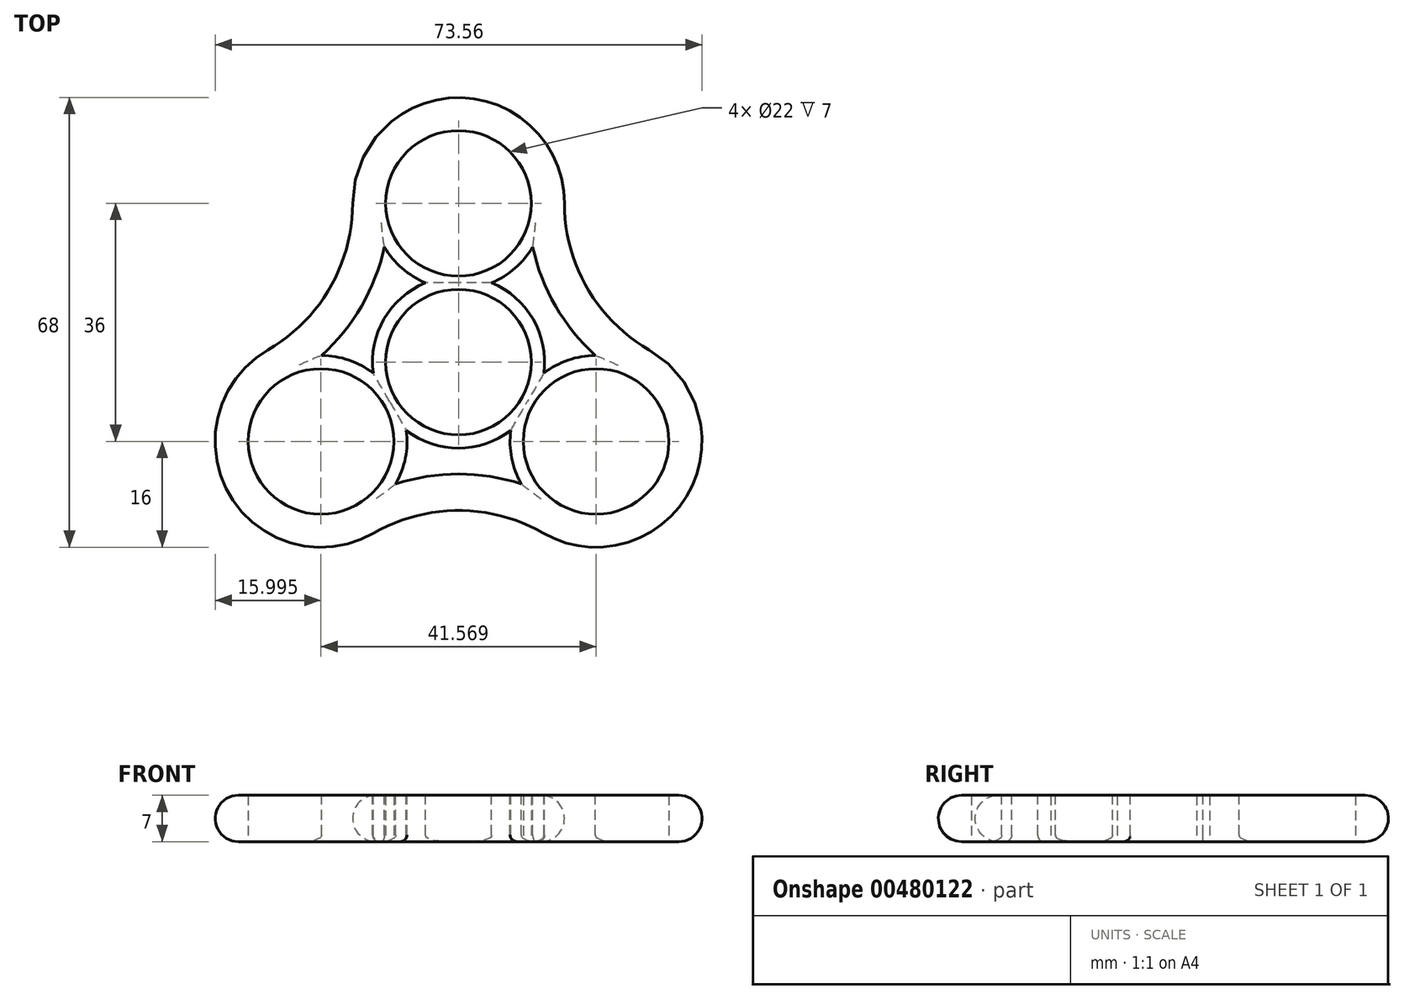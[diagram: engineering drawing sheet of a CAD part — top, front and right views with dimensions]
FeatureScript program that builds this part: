
annotation { "Feature Type Name" : "Feature", "Feature Type Description" : "" }
export const myFeature = defineFeature(function(context is Context, id is Id, definition is map)
    precondition{}
    {
        {
            var Q0;
            Q0=qCreatedBy(makeId("Top.planeOp"),FACE);
            var sketch = newSketch(context, id + "F0", { "sketchPlane" : qUnion([Q0])});
            skCircle(sketch, "E0", {"center": v(0, 0) * mm, "radius": 11 * mm});
            skArc(sketch, "E1", {"start": v(16, 24) * mm, "mid": v(0, 40) * mm, "end": v(-16, 24) * mm});
            skArc(sketch, "E2", {"start": v(16, 24) * mm, "mid": v(19.43, 11.22) * mm, "end": v(28.78, 1.86) * mm});
            skArc(sketch, "E3", {"start": v(12.78, -25.86) * mm, "mid": v(34.64, -20) * mm, "end": v(28.78, 1.86) * mm});
            skArc(sketch, "E4", {"start": v(12.78, -25.86) * mm, "mid": v(0, -22.43) * mm, "end": v(-12.78, -25.86) * mm});
            skArc(sketch, "E5", {"start": v(-28.78, 1.86) * mm, "mid": v(-34.64, -20) * mm, "end": v(-12.78, -25.86) * mm});
            skCircle(sketch, "E6", {"center": v(0, 24) * mm, "radius": 11 * mm});
            skCircle(sketch, "E7", {"center": v(20.78, -12) * mm, "radius": 11 * mm});
            skCircle(sketch, "E8", {"center": v(-20.78, -12) * mm, "radius": 11 * mm});
            skLineSegment(sketch, "E9", {"start": v(0, 0) * mm, "end": v(0, 67.7) * mm, "construction": true});
            skLineSegment(sketch, "E10", {"start": v(66.4, -38.34) * mm, "end": v(0, 0) * mm, "construction": true});
            skLineSegment(sketch, "E11", {"start": v(0, 0) * mm, "end": v(-62.05, -35.83) * mm, "construction": true});
            skArc(sketch, "E12", {"start": v(-28.78, 1.86) * mm, "mid": v(-19.43, 11.22) * mm, "end": v(-16, 24) * mm});
            skLineSegment(sketch, "E13", {"start": v(-28.78, 1.86) * mm, "end": v(-12.78, -25.86) * mm, "construction": true});
            skSolve(sketch);
        }
        {
            var Q0;
            Q0=makeQuery(id+"F0.imprint","IMPRINT",FACE,{"disambiguationData":[TD([[makeQuery(id+"F0.imprint","IMPRINT",EDGE,{"derivedFrom":sQuery(id+"F0.wireOp",EDGE,"E0")}),-1.0]])]});
            extrude(context, id + "F1", {"entities" : qUnion([Q0]), "depth" : 7 * mm});
        }
        {
            var Q0;
            Q0=makeQuery(id+"F1.opExtrude","CAP_EDGE",EDGE,{"disambiguationData":[OSD([sQuery(id+"F0.wireOp",EDGE,"E2")])],"isStart":false});
            var Q1;
            Q1=makeQuery(id+"F1.opExtrude","CAP_EDGE",EDGE,{"disambiguationData":[OSD([sQuery(id+"F0.wireOp",EDGE,"E2")])],"isStart":true});
            fillet(context, id + "F2", {"entities" : qUnion([Q0, Q1]), "radius" : 3.5 * mm, "tangentPropagation" : true, "allowEdgeOverflow" : false});
        }
        {
            var Q0;
            Q0=makeQuery(id+"F1.opExtrude","CAP_FACE",FACE,{"disambiguationData":[OSD([sQuery(id+"F0.wireOp",EDGE,"E0"),sQuery(id+"F0.wireOp",EDGE,"E1"),sQuery(id+"F0.wireOp",EDGE,"E2"),sQuery(id+"F0.wireOp",EDGE,"E3"),sQuery(id+"F0.wireOp",EDGE,"E4"),sQuery(id+"F0.wireOp",EDGE,"E5"),sQuery(id+"F0.wireOp",EDGE,"E6"),sQuery(id+"F0.wireOp",EDGE,"E7"),sQuery(id+"F0.wireOp",EDGE,"E8"),sQuery(id+"F0.wireOp",EDGE,"E12")])],"isStart":false});
            var sketch = newSketch(context, id + "F3", { "sketchPlane" : qUnion([Q0])});
            skArc(sketch, "E14", {"start": v(-5, 12) * mm, "mid": v(-11.26, 6.5) * mm, "end": v(-12.9, -1.67) * mm});
            skArc(sketch, "E15", {"start": v(-11.2, 17.41) * mm, "mid": v(-8.54, 14.2) * mm, "end": v(-5, 12) * mm});
            skArc(sketch, "E16", {"start": v(-20.68, 1) * mm, "mid": v(-14.66, 8.47) * mm, "end": v(-11.2, 17.41) * mm});
            skArc(sketch, "E17", {"start": v(-12.9, -1.67) * mm, "mid": v(-16.57, 0.3) * mm, "end": v(-20.68, 1) * mm});
            skArc(sketch, "E18.1.0", {"start": v(-7.9, -10.33) * mm, "mid": v(0, -13) * mm, "end": v(7.9, -10.33) * mm});
            skArc(sketch, "E18.1.1", {"start": v(7.9, -10.33) * mm, "mid": v(8.03, -14.5) * mm, "end": v(9.48, -18.41) * mm});
            skArc(sketch, "E18.1.2", {"start": v(-9.48, -18.41) * mm, "mid": v(-8.03, -14.5) * mm, "end": v(-7.9, -10.33) * mm});
            skArc(sketch, "E18.1.3", {"start": v(9.48, -18.41) * mm, "mid": v(0, -16.93) * mm, "end": v(-9.48, -18.41) * mm});
            skArc(sketch, "E18.2.0", {"start": v(12.9, -1.67) * mm, "mid": v(11.26, 6.5) * mm, "end": v(5, 12) * mm});
            skArc(sketch, "E18.2.1", {"start": v(5, 12) * mm, "mid": v(8.54, 14.2) * mm, "end": v(11.2, 17.41) * mm});
            skArc(sketch, "E18.2.2", {"start": v(20.68, 1) * mm, "mid": v(16.57, 0.3) * mm, "end": v(12.9, -1.67) * mm});
            skArc(sketch, "E18.2.3", {"start": v(11.2, 17.41) * mm, "mid": v(14.66, 8.47) * mm, "end": v(20.68, 1) * mm});
            skSolve(sketch);
        }
        {
            var Q0;
            Q0=makeQuery(id+"F3.imprint","IMPRINT",FACE,{"disambiguationData":[TD([[makeQuery(id+"F3.imprint","IMPRINT",EDGE,{"derivedFrom":sQuery(id+"F3.wireOp",EDGE,"E18.2.0")}),-1.0]])]});
            var Q1;
            Q1=makeQuery(id+"F3.imprint","IMPRINT",FACE,{"disambiguationData":[TD([[makeQuery(id+"F3.imprint","IMPRINT",EDGE,{"derivedFrom":sQuery(id+"F3.wireOp",EDGE,"E14")}),-1.0]])]});
            var Q2;
            Q2=makeQuery(id+"F3.imprint","IMPRINT",FACE,{"disambiguationData":[TD([[makeQuery(id+"F3.imprint","IMPRINT",EDGE,{"derivedFrom":sQuery(id+"F3.wireOp",EDGE,"E18.1.0")}),-1.0]])]});
            extrude(context, id + "F4", {"entities" : qUnion([Q0, Q1, Q2]), "operationType" : NewBodyOperationType.REMOVE, "oppositeDirection" : true, "depth" : 25 * mm});
        }
        {
            var Q0;
            Q0=makeQuery(id+"F4.boolean.opBoolean","COPY",EDGE,{"derivedFrom":makeQuery(id+"F4.opExtrude","CAP_EDGE",EDGE,{"disambiguationData":[OSD([sQuery(id+"F3.wireOp",EDGE,"E16")])],"isStart":true})});
            var Q1;
            Q1=makeQuery(id+"F4.boolean.opBoolean","COPY",EDGE,{"derivedFrom":makeQuery(id+"F4.opExtrude","CAP_EDGE",EDGE,{"disambiguationData":[OSD([sQuery(id+"F3.wireOp",EDGE,"E17")])],"isStart":true})});
            var Q2;
            Q2=makeQuery(id+"F4.boolean.opBoolean","COPY",EDGE,{"derivedFrom":makeQuery(id+"F4.opExtrude","CAP_EDGE",EDGE,{"disambiguationData":[OSD([sQuery(id+"F3.wireOp",EDGE,"E14")])],"isStart":true})});
            var Q3;
            Q3=makeQuery(id+"F4.boolean.opBoolean","COPY",EDGE,{"derivedFrom":makeQuery(id+"F4.opExtrude","CAP_EDGE",EDGE,{"disambiguationData":[OSD([sQuery(id+"F3.wireOp",EDGE,"E15")])],"isStart":true})});
            var Q4;
            Q4=makeQuery(id+"F4.boolean.opBoolean","COPY",EDGE,{"derivedFrom":makeQuery(id+"F4.opExtrude","CAP_EDGE",EDGE,{"disambiguationData":[OSD([sQuery(id+"F3.wireOp",EDGE,"E18.2.0")])],"isStart":true})});
            var Q5;
            Q5=makeQuery(id+"F4.boolean.opBoolean","COPY",EDGE,{"derivedFrom":makeQuery(id+"F4.opExtrude","CAP_EDGE",EDGE,{"disambiguationData":[OSD([sQuery(id+"F3.wireOp",EDGE,"E18.2.1")])],"isStart":true})});
            var Q6;
            Q6=makeQuery(id+"F4.boolean.opBoolean","COPY",EDGE,{"derivedFrom":makeQuery(id+"F4.opExtrude","CAP_EDGE",EDGE,{"disambiguationData":[OSD([sQuery(id+"F3.wireOp",EDGE,"E18.2.3")])],"isStart":true})});
            var Q7;
            Q7=makeQuery(id+"F4.boolean.opBoolean","COPY",EDGE,{"derivedFrom":makeQuery(id+"F4.opExtrude","CAP_EDGE",EDGE,{"disambiguationData":[OSD([sQuery(id+"F3.wireOp",EDGE,"E18.2.2")])],"isStart":true})});
            var Q8;
            Q8=makeQuery(id+"F4.boolean.opBoolean","COPY",EDGE,{"derivedFrom":makeQuery(id+"F4.opExtrude","CAP_EDGE",EDGE,{"disambiguationData":[OSD([sQuery(id+"F3.wireOp",EDGE,"E18.1.0")])],"isStart":true})});
            var Q9;
            Q9=makeQuery(id+"F4.boolean.opBoolean","COPY",EDGE,{"derivedFrom":makeQuery(id+"F4.opExtrude","CAP_EDGE",EDGE,{"disambiguationData":[OSD([sQuery(id+"F3.wireOp",EDGE,"E18.1.2")])],"isStart":true})});
            var Q10;
            Q10=makeQuery(id+"F4.boolean.opBoolean","COPY",EDGE,{"derivedFrom":makeQuery(id+"F4.opExtrude","CAP_EDGE",EDGE,{"disambiguationData":[OSD([sQuery(id+"F3.wireOp",EDGE,"E18.1.3")])],"isStart":true})});
            var Q11;
            Q11=makeQuery(id+"F4.boolean.opBoolean","COPY",EDGE,{"derivedFrom":makeQuery(id+"F4.opExtrude","CAP_EDGE",EDGE,{"disambiguationData":[OSD([sQuery(id+"F3.wireOp",EDGE,"E18.1.1")])],"isStart":true})});
            var Q12;
            Q12=makeQuery(id+"F4.boolean.opBoolean","INTERSECT",EDGE,{"derivedFrom":[makeQuery(id+"F1.opExtrude","CAP_FACE",FACE,{"disambiguationData":[OSD([sQuery(id+"F0.wireOp",EDGE,"E0"),sQuery(id+"F0.wireOp",EDGE,"E1"),sQuery(id+"F0.wireOp",EDGE,"E2"),sQuery(id+"F0.wireOp",EDGE,"E3"),sQuery(id+"F0.wireOp",EDGE,"E4"),sQuery(id+"F0.wireOp",EDGE,"E5"),sQuery(id+"F0.wireOp",EDGE,"E6"),sQuery(id+"F0.wireOp",EDGE,"E7"),sQuery(id+"F0.wireOp",EDGE,"E8"),sQuery(id+"F0.wireOp",EDGE,"E12")])],"isStart":true}),makeQuery(id+"F4.opExtrude","SWEPT_FACE",FACE,{"disambiguationData":[OSD([sQuery(id+"F3.wireOp",EDGE,"E18.2.1")])]})]});
            var Q13;
            Q13=makeQuery(id+"F4.boolean.opBoolean","INTERSECT",EDGE,{"derivedFrom":[makeQuery(id+"F1.opExtrude","CAP_FACE",FACE,{"disambiguationData":[OSD([sQuery(id+"F0.wireOp",EDGE,"E0"),sQuery(id+"F0.wireOp",EDGE,"E1"),sQuery(id+"F0.wireOp",EDGE,"E2"),sQuery(id+"F0.wireOp",EDGE,"E3"),sQuery(id+"F0.wireOp",EDGE,"E4"),sQuery(id+"F0.wireOp",EDGE,"E5"),sQuery(id+"F0.wireOp",EDGE,"E6"),sQuery(id+"F0.wireOp",EDGE,"E7"),sQuery(id+"F0.wireOp",EDGE,"E8"),sQuery(id+"F0.wireOp",EDGE,"E12")])],"isStart":true}),makeQuery(id+"F4.opExtrude","SWEPT_FACE",FACE,{"disambiguationData":[OSD([sQuery(id+"F3.wireOp",EDGE,"E18.2.0")])]})]});
            var Q14;
            Q14=makeQuery(id+"F4.boolean.opBoolean","INTERSECT",EDGE,{"derivedFrom":[makeQuery(id+"F1.opExtrude","CAP_FACE",FACE,{"disambiguationData":[OSD([sQuery(id+"F0.wireOp",EDGE,"E0"),sQuery(id+"F0.wireOp",EDGE,"E1"),sQuery(id+"F0.wireOp",EDGE,"E2"),sQuery(id+"F0.wireOp",EDGE,"E3"),sQuery(id+"F0.wireOp",EDGE,"E4"),sQuery(id+"F0.wireOp",EDGE,"E5"),sQuery(id+"F0.wireOp",EDGE,"E6"),sQuery(id+"F0.wireOp",EDGE,"E7"),sQuery(id+"F0.wireOp",EDGE,"E8"),sQuery(id+"F0.wireOp",EDGE,"E12")])],"isStart":true}),makeQuery(id+"F4.opExtrude","SWEPT_FACE",FACE,{"disambiguationData":[OSD([sQuery(id+"F3.wireOp",EDGE,"E18.2.3")])]})]});
            var Q15;
            Q15=makeQuery(id+"F4.boolean.opBoolean","INTERSECT",EDGE,{"derivedFrom":[makeQuery(id+"F1.opExtrude","CAP_FACE",FACE,{"disambiguationData":[OSD([sQuery(id+"F0.wireOp",EDGE,"E0"),sQuery(id+"F0.wireOp",EDGE,"E1"),sQuery(id+"F0.wireOp",EDGE,"E2"),sQuery(id+"F0.wireOp",EDGE,"E3"),sQuery(id+"F0.wireOp",EDGE,"E4"),sQuery(id+"F0.wireOp",EDGE,"E5"),sQuery(id+"F0.wireOp",EDGE,"E6"),sQuery(id+"F0.wireOp",EDGE,"E7"),sQuery(id+"F0.wireOp",EDGE,"E8"),sQuery(id+"F0.wireOp",EDGE,"E12")])],"isStart":true}),makeQuery(id+"F4.opExtrude","SWEPT_FACE",FACE,{"disambiguationData":[OSD([sQuery(id+"F3.wireOp",EDGE,"E18.2.2")])]})]});
            var Q16;
            Q16=makeQuery(id+"F4.boolean.opBoolean","INTERSECT",EDGE,{"derivedFrom":[makeQuery(id+"F1.opExtrude","CAP_FACE",FACE,{"disambiguationData":[OSD([sQuery(id+"F0.wireOp",EDGE,"E0"),sQuery(id+"F0.wireOp",EDGE,"E1"),sQuery(id+"F0.wireOp",EDGE,"E2"),sQuery(id+"F0.wireOp",EDGE,"E3"),sQuery(id+"F0.wireOp",EDGE,"E4"),sQuery(id+"F0.wireOp",EDGE,"E5"),sQuery(id+"F0.wireOp",EDGE,"E6"),sQuery(id+"F0.wireOp",EDGE,"E7"),sQuery(id+"F0.wireOp",EDGE,"E8"),sQuery(id+"F0.wireOp",EDGE,"E12")])],"isStart":true}),makeQuery(id+"F4.opExtrude","SWEPT_FACE",FACE,{"disambiguationData":[OSD([sQuery(id+"F3.wireOp",EDGE,"E15")])]})]});
            var Q17;
            Q17=makeQuery(id+"F4.boolean.opBoolean","INTERSECT",EDGE,{"derivedFrom":[makeQuery(id+"F1.opExtrude","CAP_FACE",FACE,{"disambiguationData":[OSD([sQuery(id+"F0.wireOp",EDGE,"E0"),sQuery(id+"F0.wireOp",EDGE,"E1"),sQuery(id+"F0.wireOp",EDGE,"E2"),sQuery(id+"F0.wireOp",EDGE,"E3"),sQuery(id+"F0.wireOp",EDGE,"E4"),sQuery(id+"F0.wireOp",EDGE,"E5"),sQuery(id+"F0.wireOp",EDGE,"E6"),sQuery(id+"F0.wireOp",EDGE,"E7"),sQuery(id+"F0.wireOp",EDGE,"E8"),sQuery(id+"F0.wireOp",EDGE,"E12")])],"isStart":true}),makeQuery(id+"F4.opExtrude","SWEPT_FACE",FACE,{"disambiguationData":[OSD([sQuery(id+"F3.wireOp",EDGE,"E14")])]})]});
            var Q18;
            Q18=makeQuery(id+"F4.boolean.opBoolean","INTERSECT",EDGE,{"derivedFrom":[makeQuery(id+"F1.opExtrude","CAP_FACE",FACE,{"disambiguationData":[OSD([sQuery(id+"F0.wireOp",EDGE,"E0"),sQuery(id+"F0.wireOp",EDGE,"E1"),sQuery(id+"F0.wireOp",EDGE,"E2"),sQuery(id+"F0.wireOp",EDGE,"E3"),sQuery(id+"F0.wireOp",EDGE,"E4"),sQuery(id+"F0.wireOp",EDGE,"E5"),sQuery(id+"F0.wireOp",EDGE,"E6"),sQuery(id+"F0.wireOp",EDGE,"E7"),sQuery(id+"F0.wireOp",EDGE,"E8"),sQuery(id+"F0.wireOp",EDGE,"E12")])],"isStart":true}),makeQuery(id+"F4.opExtrude","SWEPT_FACE",FACE,{"disambiguationData":[OSD([sQuery(id+"F3.wireOp",EDGE,"E16")])]})]});
            var Q19;
            Q19=makeQuery(id+"F4.boolean.opBoolean","INTERSECT",EDGE,{"derivedFrom":[makeQuery(id+"F1.opExtrude","CAP_FACE",FACE,{"disambiguationData":[OSD([sQuery(id+"F0.wireOp",EDGE,"E0"),sQuery(id+"F0.wireOp",EDGE,"E1"),sQuery(id+"F0.wireOp",EDGE,"E2"),sQuery(id+"F0.wireOp",EDGE,"E3"),sQuery(id+"F0.wireOp",EDGE,"E4"),sQuery(id+"F0.wireOp",EDGE,"E5"),sQuery(id+"F0.wireOp",EDGE,"E6"),sQuery(id+"F0.wireOp",EDGE,"E7"),sQuery(id+"F0.wireOp",EDGE,"E8"),sQuery(id+"F0.wireOp",EDGE,"E12")])],"isStart":true}),makeQuery(id+"F4.opExtrude","SWEPT_FACE",FACE,{"disambiguationData":[OSD([sQuery(id+"F3.wireOp",EDGE,"E17")])]})]});
            var Q20;
            Q20=makeQuery(id+"F4.boolean.opBoolean","INTERSECT",EDGE,{"derivedFrom":[makeQuery(id+"F1.opExtrude","CAP_FACE",FACE,{"disambiguationData":[OSD([sQuery(id+"F0.wireOp",EDGE,"E0"),sQuery(id+"F0.wireOp",EDGE,"E1"),sQuery(id+"F0.wireOp",EDGE,"E2"),sQuery(id+"F0.wireOp",EDGE,"E3"),sQuery(id+"F0.wireOp",EDGE,"E4"),sQuery(id+"F0.wireOp",EDGE,"E5"),sQuery(id+"F0.wireOp",EDGE,"E6"),sQuery(id+"F0.wireOp",EDGE,"E7"),sQuery(id+"F0.wireOp",EDGE,"E8"),sQuery(id+"F0.wireOp",EDGE,"E12")])],"isStart":true}),makeQuery(id+"F4.opExtrude","SWEPT_FACE",FACE,{"disambiguationData":[OSD([sQuery(id+"F3.wireOp",EDGE,"E18.1.2")])]})]});
            var Q21;
            Q21=makeQuery(id+"F4.boolean.opBoolean","INTERSECT",EDGE,{"derivedFrom":[makeQuery(id+"F1.opExtrude","CAP_FACE",FACE,{"disambiguationData":[OSD([sQuery(id+"F0.wireOp",EDGE,"E0"),sQuery(id+"F0.wireOp",EDGE,"E1"),sQuery(id+"F0.wireOp",EDGE,"E2"),sQuery(id+"F0.wireOp",EDGE,"E3"),sQuery(id+"F0.wireOp",EDGE,"E4"),sQuery(id+"F0.wireOp",EDGE,"E5"),sQuery(id+"F0.wireOp",EDGE,"E6"),sQuery(id+"F0.wireOp",EDGE,"E7"),sQuery(id+"F0.wireOp",EDGE,"E8"),sQuery(id+"F0.wireOp",EDGE,"E12")])],"isStart":true}),makeQuery(id+"F4.opExtrude","SWEPT_FACE",FACE,{"disambiguationData":[OSD([sQuery(id+"F3.wireOp",EDGE,"E18.1.3")])]})]});
            var Q22;
            Q22=makeQuery(id+"F4.boolean.opBoolean","INTERSECT",EDGE,{"derivedFrom":[makeQuery(id+"F1.opExtrude","CAP_FACE",FACE,{"disambiguationData":[OSD([sQuery(id+"F0.wireOp",EDGE,"E0"),sQuery(id+"F0.wireOp",EDGE,"E1"),sQuery(id+"F0.wireOp",EDGE,"E2"),sQuery(id+"F0.wireOp",EDGE,"E3"),sQuery(id+"F0.wireOp",EDGE,"E4"),sQuery(id+"F0.wireOp",EDGE,"E5"),sQuery(id+"F0.wireOp",EDGE,"E6"),sQuery(id+"F0.wireOp",EDGE,"E7"),sQuery(id+"F0.wireOp",EDGE,"E8"),sQuery(id+"F0.wireOp",EDGE,"E12")])],"isStart":true}),makeQuery(id+"F4.opExtrude","SWEPT_FACE",FACE,{"disambiguationData":[OSD([sQuery(id+"F3.wireOp",EDGE,"E18.1.1")])]})]});
            var Q23;
            Q23=makeQuery(id+"F4.boolean.opBoolean","INTERSECT",EDGE,{"derivedFrom":[makeQuery(id+"F1.opExtrude","CAP_FACE",FACE,{"disambiguationData":[OSD([sQuery(id+"F0.wireOp",EDGE,"E0"),sQuery(id+"F0.wireOp",EDGE,"E1"),sQuery(id+"F0.wireOp",EDGE,"E2"),sQuery(id+"F0.wireOp",EDGE,"E3"),sQuery(id+"F0.wireOp",EDGE,"E4"),sQuery(id+"F0.wireOp",EDGE,"E5"),sQuery(id+"F0.wireOp",EDGE,"E6"),sQuery(id+"F0.wireOp",EDGE,"E7"),sQuery(id+"F0.wireOp",EDGE,"E8"),sQuery(id+"F0.wireOp",EDGE,"E12")])],"isStart":true}),makeQuery(id+"F4.opExtrude","SWEPT_FACE",FACE,{"disambiguationData":[OSD([sQuery(id+"F3.wireOp",EDGE,"E18.1.0")])]})]});
            fillet(context, id + "F5", {"entities" : qUnion([Q0, Q1, Q2, Q3, Q4, Q5, Q6, Q7, Q8, Q9, Q10, Q11, Q12, Q13, Q14, Q15, Q16, Q17, Q18, Q19, Q20, Q21, Q22, Q23]), "radius" : 1 * mm, "tangentPropagation" : true, "allowEdgeOverflow" : false});
        }
    });
